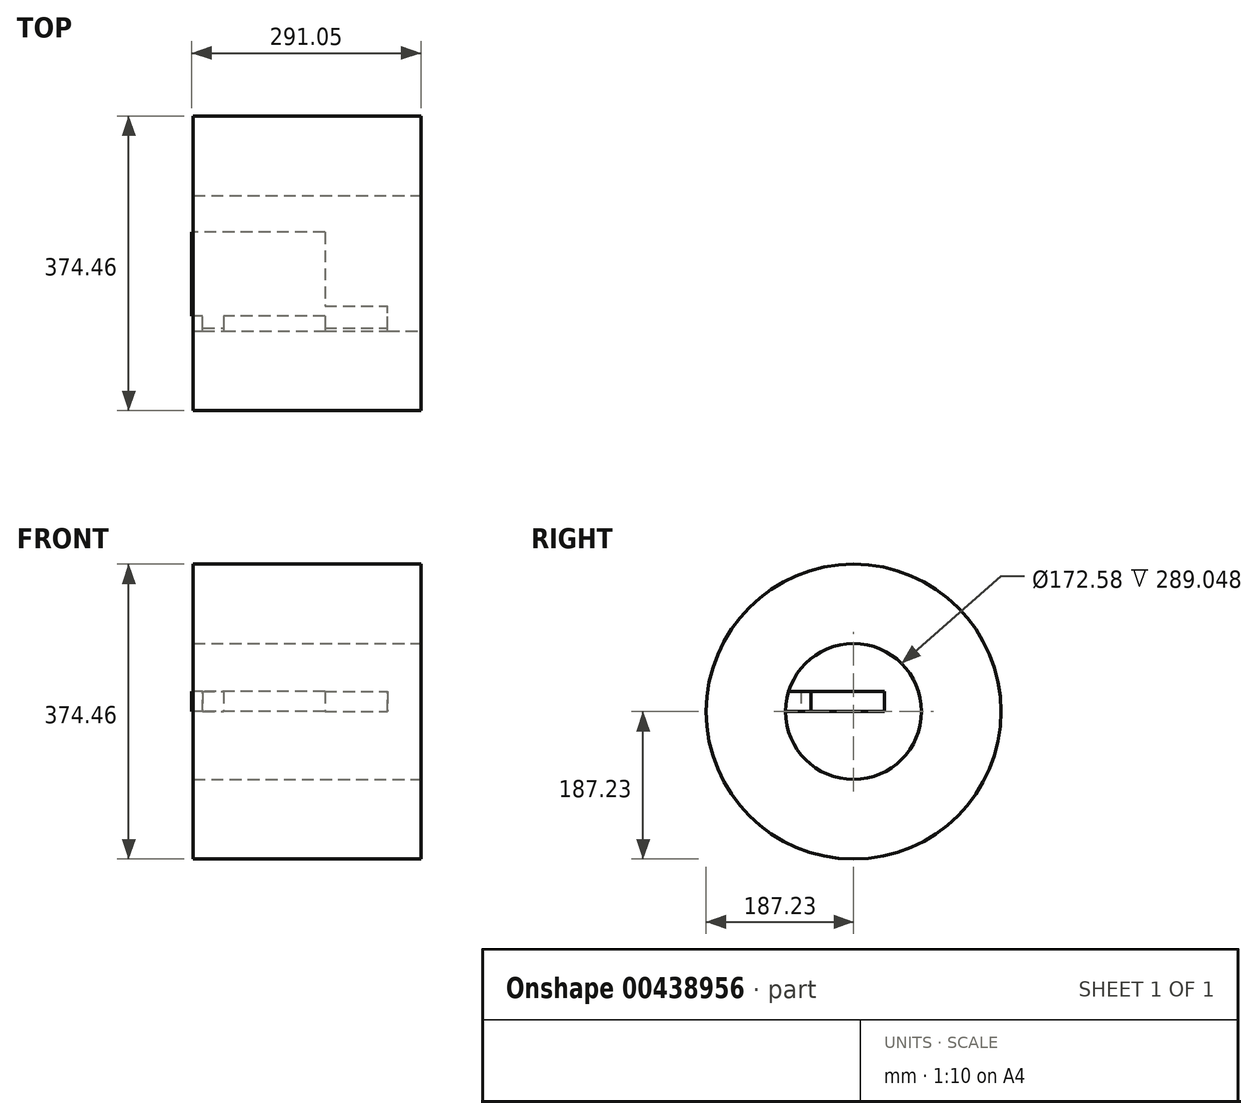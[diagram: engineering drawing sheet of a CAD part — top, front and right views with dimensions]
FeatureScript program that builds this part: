
annotation { "Feature Type Name" : "Feature", "Feature Type Description" : "" }
export const myFeature = defineFeature(function(context is Context, id is Id, definition is map)
    precondition{}
    {
        {
            var Q0;
            Q0=qCreatedBy(makeId("Top.planeOp"),FACE);
            var sketch = newSketch(context, id + "F0", { "sketchPlane" : qUnion([Q0])});
            skLineSegment(sketch, "E0.bottom", {"start": v(-11.74, 0) * mm, "end": v(117, 0) * mm});
            skLineSegment(sketch, "E0.top", {"start": v(-11.74, -99.1) * mm, "end": v(117, -99.1) * mm});
            skLineSegment(sketch, "E0.left", {"start": v(-11.74, 0) * mm, "end": v(-11.74, -99.1) * mm});
            skLineSegment(sketch, "E0.right", {"start": v(117, 0) * mm, "end": v(117, -99.1) * mm});
            skPoint(sketch, "E0.middle", {"position": v(52.63, -49.55) * mm});
            skLineSegment(sketch, "E1.bottom", {"start": v(117, -66.7) * mm, "end": v(-52.17, -66.7) * mm});
            skLineSegment(sketch, "E1.top", {"start": v(117, 39.43) * mm, "end": v(-52.17, 39.43) * mm});
            skLineSegment(sketch, "E1.left", {"start": v(117, -66.7) * mm, "end": v(117, 39.43) * mm});
            skLineSegment(sketch, "E1.right", {"start": v(-52.17, -66.7) * mm, "end": v(-52.17, 39.43) * mm});
            skPoint(sketch, "E1.middle", {"position": v(32.42, -13.64) * mm});
            skLineSegment(sketch, "E2.bottom", {"start": v(-38.16, -138.34) * mm, "end": v(196.62, -138.34) * mm});
            skLineSegment(sketch, "E2.top", {"start": v(-38.16, -54.03) * mm, "end": v(196.62, -54.03) * mm});
            skLineSegment(sketch, "E2.left", {"start": v(-38.16, -138.34) * mm, "end": v(-38.16, -54.03) * mm});
            skLineSegment(sketch, "E2.right", {"start": v(196.62, -138.34) * mm, "end": v(196.62, -54.03) * mm});
            skPoint(sketch, "E2.middle", {"position": v(79.23, -96.19) * mm});
            skSolve(sketch);
        }
        {
            var Q0;
            Q0 = qSketchRegion(id + "F0", true);
            extrude(context, id + "F1", {"entities" : qUnion([Q0]), "depth" : 25.4 * mm});
        }
        {
            var Q0;
            Q0=qCreatedBy(makeId("Front.planeOp"),FACE);
            var sketch = newSketch(context, id + "F2", { "sketchPlane" : qUnion([Q0])});
            skLineSegment(sketch, "E3.bottom", {"start": v(238.88, 86.29) * mm, "end": v(-50.17, 86.29) * mm});
            skLineSegment(sketch, "E3.top", {"start": v(238.88, 187.23) * mm, "end": v(-50.17, 187.23) * mm});
            skLineSegment(sketch, "E3.left", {"start": v(238.88, 86.29) * mm, "end": v(238.88, 187.23) * mm});
            skLineSegment(sketch, "E3.right", {"start": v(-50.17, 86.29) * mm, "end": v(-50.17, 187.23) * mm});
            skLineSegment(sketch, "E4.bottom", {"start": v(689.2, 0) * mm, "end": v(0, 0) * mm, "construction": true});
            skLineSegment(sketch, "E4.top", {"start": v(689.2, 239.85) * mm, "end": v(0, 239.85) * mm, "construction": true});
            skLineSegment(sketch, "E4.left", {"start": v(689.2, 0) * mm, "end": v(689.2, 239.85) * mm, "construction": true});
            skLineSegment(sketch, "E4.right", {"start": v(0, 0) * mm, "end": v(0, 239.85) * mm, "construction": true});
            skSolve(sketch);
        }
        {
            var Q0;
            Q0=makeQuery(id+"F2.imprint","IMPRINT",FACE,{"disambiguationData":[TD([[makeQuery(id+"F2.imprint","IMPRINT",EDGE,{"derivedFrom":sQuery(id+"F2.wireOp",EDGE,"E3.bottom")}),-1.0]])]});
            var Q1;
            Q1=sQuery(id+"F2.wireOp",EDGE,"E4.bottom");
            revolve(context, id + "F3", {"operationType" : NewBodyOperationType.ADD, "entities" : qUnion([Q0]), "axis" : qUnion([Q1]), "revolveType" : RevolveType.FULL});
        }
    });
